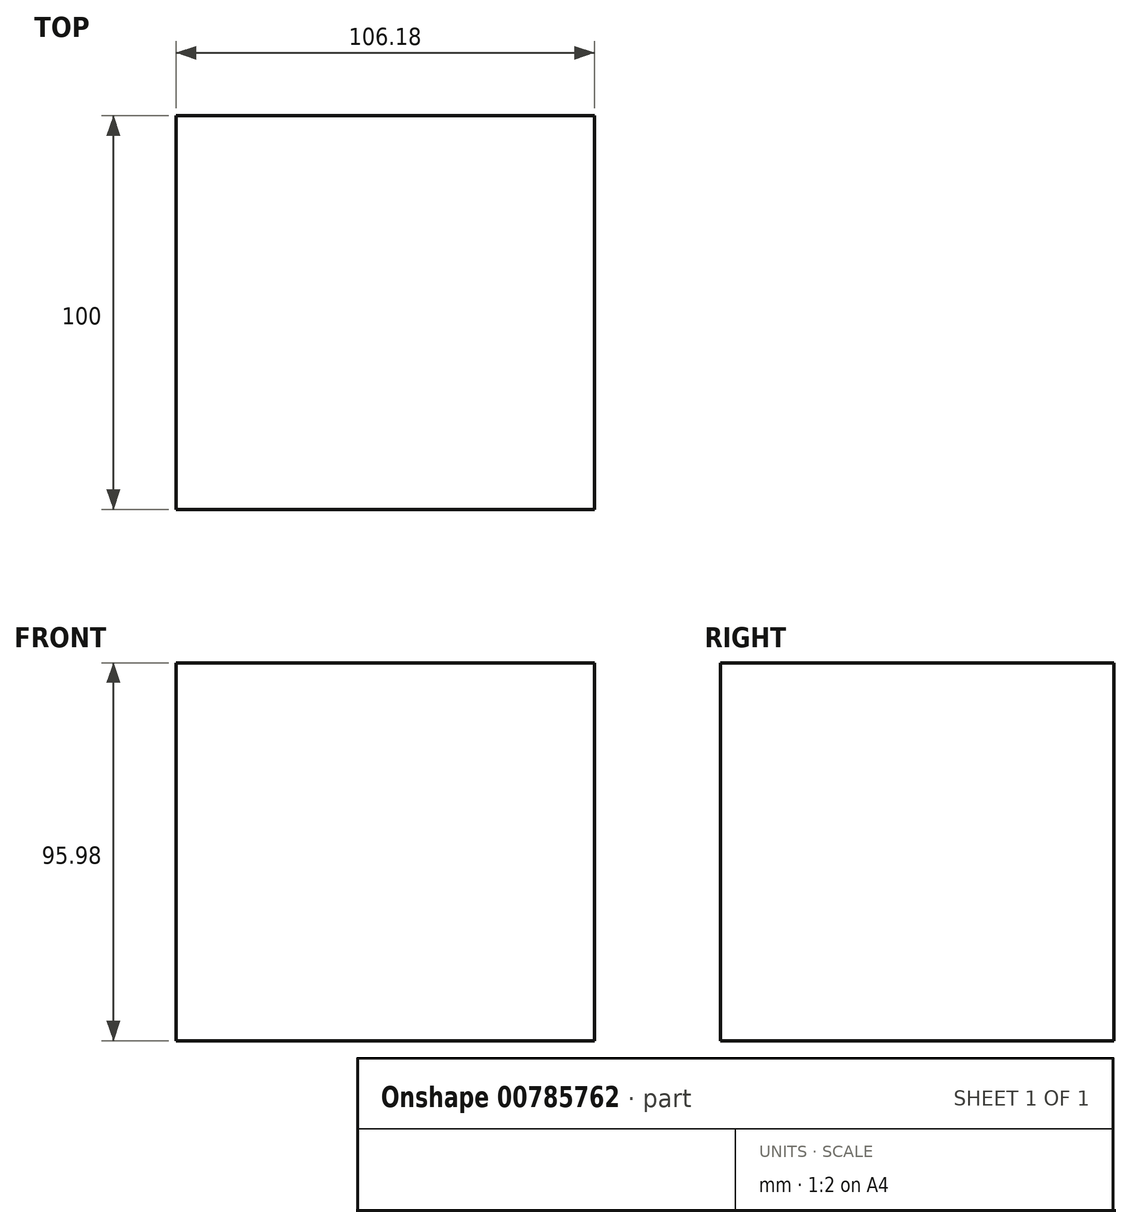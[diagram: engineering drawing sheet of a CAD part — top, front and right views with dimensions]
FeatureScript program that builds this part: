
annotation { "Feature Type Name" : "Feature", "Feature Type Description" : "" }
export const myFeature = defineFeature(function(context is Context, id is Id, definition is map)
    precondition{}
    {
        {
            var Q0;
            Q0=qCreatedBy(makeId("Front.planeOp"),FACE);
            var sketch = newSketch(context, id + "F0", { "sketchPlane" : qUnion([Q0])});
            skLineSegment(sketch, "E0.bottom", {"start": v(53.1, -48) * mm, "end": v(-53.1, -48) * mm});
            skLineSegment(sketch, "E0.top", {"start": v(53.1, 48) * mm, "end": v(-53.1, 48) * mm});
            skLineSegment(sketch, "E0.left", {"start": v(53.1, -48) * mm, "end": v(53.1, 48) * mm});
            skLineSegment(sketch, "E0.right", {"start": v(-53.1, -48) * mm, "end": v(-53.1, 48) * mm});
            skPoint(sketch, "E0.middle", {"position": v(0, 0) * mm});
            skSolve(sketch);
        }
        {
            var Q0;
            Q0=makeQuery(id+"F0.imprint","IMPRINT",FACE,{"disambiguationData":[TD([[makeQuery(id+"F0.imprint","IMPRINT",EDGE,{"derivedFrom":sQuery(id+"F0.wireOp",EDGE,"E0.bottom")}),-1.0]])]});
            extrude(context, id + "F1", {"entities" : qUnion([Q0]), "depth" : 50 * mm, "offsetDistance" : 25 * mm, "hasSecondDirection" : true, "secondDirectionOppositeDirection" : true, "secondDirectionDepth" : 50 * mm});
        }
    });
